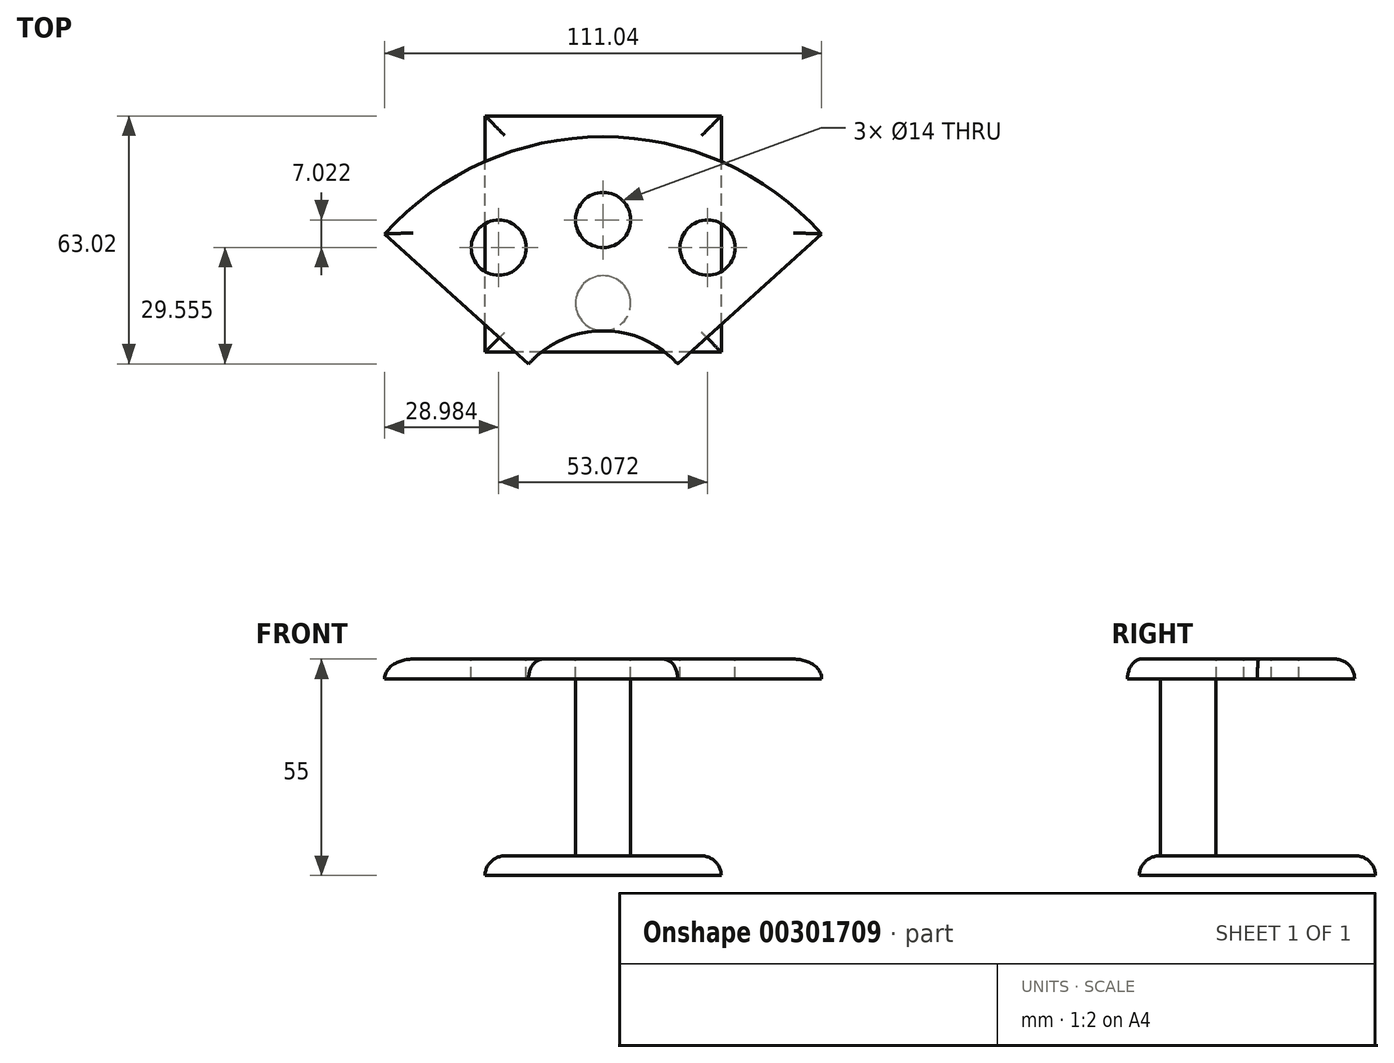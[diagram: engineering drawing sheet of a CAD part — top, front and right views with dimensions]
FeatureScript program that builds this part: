
annotation { "Feature Type Name" : "Feature", "Feature Type Description" : "" }
export const myFeature = defineFeature(function(context is Context, id is Id, definition is map)
    precondition{}
    {
        {
            var Q0;
            Q0=qCreatedBy(makeId("Top.planeOp"),FACE);
            var sketch = newSketch(context, id + "F0", { "sketchPlane" : qUnion([Q0])});
            skLineSegment(sketch, "E0.bottom", {"start": v(30, -30) * mm, "end": v(-30, -30) * mm});
            skLineSegment(sketch, "E0.top", {"start": v(30, 30) * mm, "end": v(-30, 30) * mm});
            skLineSegment(sketch, "E0.left", {"start": v(30, -30) * mm, "end": v(30, 30) * mm});
            skLineSegment(sketch, "E0.right", {"start": v(-30, -30) * mm, "end": v(-30, 30) * mm});
            skPoint(sketch, "E0.middle", {"position": v(0, 0) * mm});
            skSolve(sketch);
        }
        {
            var Q0;
            Q0=makeQuery(id+"F0.imprint","IMPRINT",FACE,{"disambiguationData":[TD([[makeQuery(id+"F0.imprint","IMPRINT",EDGE,{"derivedFrom":sQuery(id+"F0.wireOp",EDGE,"E0.bottom")}),-1.0]])]});
            extrude(context, id + "F1", {"entities" : qUnion([Q0]), "depth" : 5 * mm});
        }
        {
            var Q0;
            Q0=makeQuery(id+"F1.opExtrude","CAP_EDGE",EDGE,{"disambiguationData":[OSD([sQuery(id+"F0.wireOp",EDGE,"E0.right")])],"isStart":false});
            var Q1;
            Q1=makeQuery(id+"F1.opExtrude","CAP_EDGE",EDGE,{"disambiguationData":[OSD([sQuery(id+"F0.wireOp",EDGE,"E0.bottom")])],"isStart":false});
            var Q2;
            Q2=makeQuery(id+"F1.opExtrude","CAP_EDGE",EDGE,{"disambiguationData":[OSD([sQuery(id+"F0.wireOp",EDGE,"E0.left")])],"isStart":false});
            var Q3;
            Q3=makeQuery(id+"F1.opExtrude","CAP_EDGE",EDGE,{"disambiguationData":[OSD([sQuery(id+"F0.wireOp",EDGE,"E0.top")])],"isStart":false});
            fillet(context, id + "F2", {"entities" : qUnion([Q0, Q1, Q2, Q3]), "radius" : 5 * mm, "tangentPropagation" : true, "allowEdgeOverflow" : false});
        }
        {
            var Q0;
            Q0=makeQuery(id+"F1.opExtrude","CAP_FACE",FACE,{"disambiguationData":[OSD([sQuery(id+"F0.wireOp",EDGE,"E0.bottom"),sQuery(id+"F0.wireOp",EDGE,"E0.top"),sQuery(id+"F0.wireOp",EDGE,"E0.left"),sQuery(id+"F0.wireOp",EDGE,"E0.right")])],"isStart":false});
            var sketch = newSketch(context, id + "F3", { "sketchPlane" : qUnion([Q0])});
            skCircle(sketch, "E1", {"center": v(0, -17.6) * mm, "radius": 7 * mm});
            skSolve(sketch);
        }
        {
            var Q0;
            Q0=makeQuery(id+"F3.imprint","IMPRINT",FACE,{"disambiguationData":[TD([[makeQuery(id+"F3.imprint","IMPRINT",EDGE,{"derivedFrom":sQuery(id+"F3.wireOp",EDGE,"E1")}),1.0]])]});
            extrude(context, id + "F4", {"entities" : qUnion([Q0]), "operationType" : NewBodyOperationType.ADD, "depth" : 45 * mm});
        }
        {
            var Q0;
            Q0=makeQuery(id+"F4.opExtrude","CAP_FACE",FACE,{"disambiguationData":[OSD([sQuery(id+"F3.wireOp",EDGE,"E1")])],"isStart":false});
            var sketch = newSketch(context, id + "F5", { "sketchPlane" : qUnion([Q0])});
            skCircle(sketch, "E2", {"center": v(0, -50.1) * mm, "radius": 74.78 * mm});
            skCircle(sketch, "E3", {"center": v(0, -50.1) * mm, "radius": 25.49 * mm});
            skLineSegment(sketch, "E4", {"start": v(0, -50.1) * mm, "end": v(-55.52, 0) * mm});
            skLineSegment(sketch, "E5", {"start": v(0, -50.1) * mm, "end": v(55.52, 0) * mm});
            skSolve(sketch);
        }
        {
            var Q0;
            {var subQ5=makeQuery(id+"F4.opExtrude","CAP_EDGE",EDGE,{"disambiguationData":[OSD([sQuery(id+"F3.wireOp",EDGE,"E1")])],"isStart":false});Q0=makeQuery(id+"F5.imprint","IMPRINT",FACE,{"disambiguationData":[TD([[makeQuery(id+"F5.imprint","IMPRINT",EDGE,{"derivedFrom":subQ5}),-1.0]])]});}
            var Q1;
            Q1=makeQuery(id+"F5.imprint","IMPRINT",FACE,{"disambiguationData":[TD([[makeQuery(id+"F5.imprint","IMPRINT",EDGE,{"derivedFrom":makeQuery(id+"F4.opExtrude","CAP_EDGE",EDGE,{"disambiguationData":[OSD([sQuery(id+"F3.wireOp",EDGE,"E1")])],"isStart":false})}),1.0]])]});
            extrude(context, id + "F6", {"entities" : qUnion([Q0, Q1]), "operationType" : NewBodyOperationType.ADD, "depth" : 5 * mm});
        }
        {
            var Q0;
            Q0=makeQuery(id+"F6.opExtrude","CAP_FACE",FACE,{"disambiguationData":[OSD([sQuery(id+"F5.wireOp",EDGE,"E2"),sQuery(id+"F5.wireOp",EDGE,"E3"),sQuery(id+"F5.wireOp",EDGE,"E4"),sQuery(id+"F5.wireOp",EDGE,"E5")])],"isStart":false});
            var sketch = newSketch(context, id + "F7", { "sketchPlane" : qUnion([Q0])});
            skCircle(sketch, "E6", {"center": v(0, -50.1) * mm, "radius": 53.65 * mm});
            skCircle(sketch, "E7", {"center": v(0, 3.56) * mm, "radius": 7 * mm});
            skCircle(sketch, "E8", {"center": v(-26.54, -3.47) * mm, "radius": 7 * mm});
            skPoint(sketch, "E9", {"position": v(26.54, -3.47) * mm});
            skCircle(sketch, "E10", {"center": v(26.54, -3.47) * mm, "radius": 7 * mm});
            skSolve(sketch);
        }
        {
            var Q0;
            {var subQ0=sQuery(id+"F7.wireOp",EDGE,"E8");var subQ1=sQuery(id+"F7.wireOp",EDGE,"E6");var subQ2=makeQuery(id+"F7.imprint","INTERSECT",VERTEX,{"disambiguationData":[OD(0.0)],"derivedFrom":[subQ1,subQ0]});Q0=makeQuery(id+"F7.imprint","IMPRINT",FACE,{"disambiguationData":[TD([[makeQuery(id+"F7.imprint","IMPRINT",EDGE,{"disambiguationData":[TD([[subQ2,-1.0]])],"derivedFrom":subQ1}),1.0]])]});}
            var Q1;
            {var subQ0=sQuery(id+"F7.wireOp",EDGE,"E8");var subQ1=sQuery(id+"F7.wireOp",EDGE,"E6");var subQ2=makeQuery(id+"F7.imprint","INTERSECT",VERTEX,{"disambiguationData":[OD(0.0)],"derivedFrom":[subQ1,subQ0]});Q1=makeQuery(id+"F7.imprint","IMPRINT",FACE,{"disambiguationData":[TD([[makeQuery(id+"F7.imprint","IMPRINT",EDGE,{"disambiguationData":[TD([[subQ2,-1.0]])],"derivedFrom":subQ1}),-1.0]])]});}
            var Q2;
            {var subQ0=sQuery(id+"F7.wireOp",EDGE,"E7");var subQ1=sQuery(id+"F7.wireOp",EDGE,"E6");var subQ2=makeQuery(id+"F7.imprint","INTERSECT",VERTEX,{"disambiguationData":[OD(0.0)],"derivedFrom":[subQ1,subQ0]});Q2=makeQuery(id+"F7.imprint","IMPRINT",FACE,{"disambiguationData":[TD([[makeQuery(id+"F7.imprint","IMPRINT",EDGE,{"disambiguationData":[TD([[subQ2,-1.0]])],"derivedFrom":subQ1}),-1.0]])]});}
            var Q3;
            {var subQ0=sQuery(id+"F7.wireOp",EDGE,"E7");var subQ1=sQuery(id+"F7.wireOp",EDGE,"E6");var subQ2=makeQuery(id+"F7.imprint","INTERSECT",VERTEX,{"disambiguationData":[OD(0.0)],"derivedFrom":[subQ1,subQ0]});Q3=makeQuery(id+"F7.imprint","IMPRINT",FACE,{"disambiguationData":[TD([[makeQuery(id+"F7.imprint","IMPRINT",EDGE,{"disambiguationData":[TD([[subQ2,-1.0]])],"derivedFrom":subQ1}),1.0]])]});}
            var Q4;
            {var subQ0=sQuery(id+"F7.wireOp",EDGE,"E10");var subQ1=sQuery(id+"F7.wireOp",EDGE,"E6");var subQ2=makeQuery(id+"F7.imprint","INTERSECT",VERTEX,{"disambiguationData":[OD(0.0)],"derivedFrom":[subQ1,subQ0]});Q4=makeQuery(id+"F7.imprint","IMPRINT",FACE,{"disambiguationData":[TD([[makeQuery(id+"F7.imprint","IMPRINT",EDGE,{"disambiguationData":[TD([[subQ2,-1.0]])],"derivedFrom":subQ1}),1.0]])]});}
            var Q5;
            {var subQ0=sQuery(id+"F7.wireOp",EDGE,"E10");var subQ1=sQuery(id+"F7.wireOp",EDGE,"E6");var subQ2=makeQuery(id+"F7.imprint","INTERSECT",VERTEX,{"disambiguationData":[OD(0.0)],"derivedFrom":[subQ1,subQ0]});Q5=makeQuery(id+"F7.imprint","IMPRINT",FACE,{"disambiguationData":[TD([[makeQuery(id+"F7.imprint","IMPRINT",EDGE,{"disambiguationData":[TD([[subQ2,-1.0]])],"derivedFrom":subQ1}),-1.0]])]});}
            extrude(context, id + "F8", {"entities" : qUnion([Q0, Q1, Q2, Q3, Q4, Q5]), "operationType" : NewBodyOperationType.REMOVE, "endBound" : BoundingType.UP_TO_NEXT, "oppositeDirection" : true, "depth" : 25 * mm});
        }
        {
            var Q0;
            Q0=makeQuery(id+"F6.opExtrude","CAP_EDGE",EDGE,{"disambiguationData":[OSD([sQuery(id+"F5.wireOp",EDGE,"E5")])],"isStart":false});
            var Q1;
            Q1=makeQuery(id+"F6.opExtrude","CAP_EDGE",EDGE,{"disambiguationData":[OSD([sQuery(id+"F5.wireOp",EDGE,"E2")])],"isStart":false});
            var Q2;
            Q2=makeQuery(id+"F6.opExtrude","CAP_EDGE",EDGE,{"disambiguationData":[OSD([sQuery(id+"F5.wireOp",EDGE,"E4")])],"isStart":false});
            fillet(context, id + "F9", {"entities" : qUnion([Q0, Q1, Q2]), "radius" : 5 * mm, "tangentPropagation" : true, "allowEdgeOverflow" : false});
        }
    });
